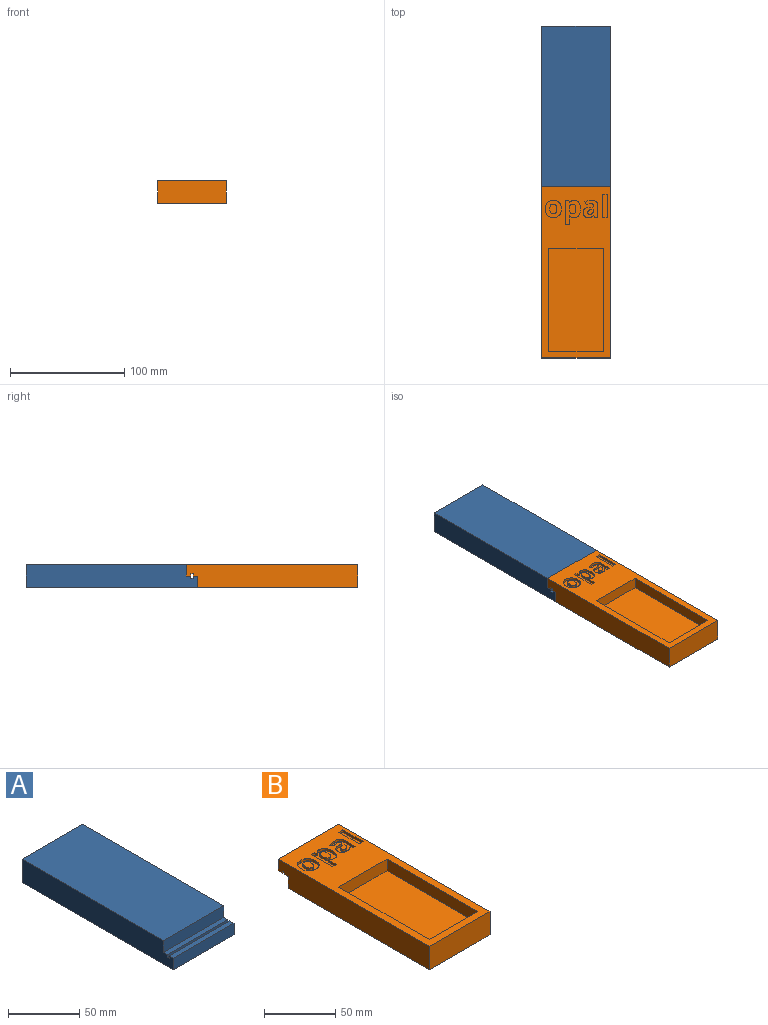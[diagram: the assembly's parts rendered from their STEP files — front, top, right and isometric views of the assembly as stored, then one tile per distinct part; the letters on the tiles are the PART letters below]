
ASSEMBLY  parts=2 mates=1
PART A: 12 faces, bbox 60x150x20 mm
  f0: plane 60x4mm, normal (0,0,1), area 240mm2, adj f1,f2,f5,f9
  f1: plane 150x20mm, normal (1,0,0), area 2896mm2, adj f0,f2,f3,f4,f6,f7,f8,f9
  f2: plane 60x10mm, normal (0,-1,0), area 600mm2, adj f0,f1,f5,f6
  f3: plane 140x60mm, normal (0,0,1), area 8400mm2, adj f1,f4,f5,f8
  f4: plane 60x20mm, normal (0,1,0), area 1200mm2, adj f1,f3,f5,f6
  f5: plane 150x20mm, normal (-1,0,0), area 2896mm2, adj f0,f2,f3,f4,f6,f7,f8,f9
  f6: plane 150x60mm, normal (0,0,-1), area 9000mm2, adj f1,f2,f4,f5
  f7: plane 60x4mm, normal (0,0,1), area 240mm2, adj f1,f5,f8,f10
  f8: plane 60x10mm, normal (0,-1,0), area 600mm2, adj f1,f3,f5,f7
  f9: plane 60x2mm, normal (0,1,0), area 120mm2, adj f0,f1,f5,f11
  f10: plane 60x2mm, normal (0,-1,0), area 120mm2, adj f1,f5,f7,f11
  f11: plane 60x2mm, normal (0,0,1), area 120mm2, adj f1,f5,f9,f10
PART B: 94 faces, bbox 60x150x20 mm
  f0: plane 60x4mm, normal (0,0,-1), area 240mm2, adj f1,f3,f4,f91
  f1: plane 150x20mm, normal (1,0,0), area 2896mm2, adj f0,f2,f3,f5,f6,f12,f13,f91
  f2: plane 150x60mm, normal (0,0,1), area 4078mm2, adj f1,f3,f4,f5,f7,f8,f9,f10
  f3: plane 60x10mm, normal (0,1,0), area 600mm2, adj f0,f1,f2,f4
  f4: plane 150x20mm, normal (-1,0,0), area 2896mm2, adj f0,f2,f3,f5,f6,f12,f13,f91
  f5: plane 60x20mm, normal (0,-1,0), area 1200mm2, adj f1,f2,f4,f6
  f6: plane 140x60mm, normal (0,0,-1), area 8400mm2, adj f1,f4,f5,f13
  f7: plane 48x10mm, normal (0,-1,0), area 480mm2, adj f2,f8,f10,f11
  f8: plane 90x10mm, normal (1,0,0), area 900mm2, adj f2,f7,f9,f11
  f9: plane 48x10mm, normal (0,1,0), area 480mm2, adj f2,f8,f10,f11
  f10: plane 90x10mm, normal (-1,0,0), area 900mm2, adj f2,f7,f9,f11
  f11: plane 90x48mm, normal (0,0,1), area 4320mm2, adj f7,f8,f9,f10
  f12: plane 60x4mm, normal (0,0,-1), area 240mm2, adj f1,f4,f13,f92
  f13: plane 60x10mm, normal (0,1,0), area 600mm2, adj f1,f4,f6,f12
  f14: plane 2x1.53mm, normal (-0.04,1,0), area 3.1mm2, adj f15,f38,f39,f89
  f15: plane 2x1.19mm, normal (1,0,0), area 2.4mm2, adj f14,f16,f39,f89
  f16: extruded ~2.1x2mm, area 4.6mm2, adj f15,f17,f39,f89
  f17: extruded ~2.2x2mm, area 4.8mm2, adj f16,f18,f39,f89
  f18: extruded ~2x1.92mm, area 5.8mm2, adj f17,f19,f39,f89
  f19: extruded ~2x1.74mm, area 4mm2, adj f18,f38,f39,f89
  f20: plane 2x1.97mm, normal (0.93,0.36,0), area 4.2mm2, adj f2,f21,f37,f39
  f21: plane 2.76x2mm, normal (0,1,0), area 5.5mm2, adj f2,f20,f22,f39
  f22: plane 9.65x2mm, normal (-1,0,0), area 19.3mm2, adj f2,f21,f23,f39
  f23: extruded ~3.86x2mm, area 8.6mm2, adj f2,f22,f24,f39
  f24: extruded ~4.47x2mm, area 9.5mm2, adj f2,f23,f25,f39
  f25: extruded ~5.54x2mm, area 11.5mm2, adj f2,f24,f26,f39
  f26: plane 2.67x2mm, normal (0.9,0.44,0), area 5.9mm2, adj f2,f25,f27,f39
  f27: extruded ~4.08x2mm, area 8.5mm2, adj f2,f26,f28,f39
  f28: extruded ~2.26x2.2mm, area 7.2mm2, adj f2,f27,f29,f39
  f29: plane 2x0.63mm, normal (1,0,0), area 1.3mm2, adj f2,f28,f30,f39
  f30: plane 2.52x2mm, normal (0.03,-1,0), area 5mm2, adj f2,f29,f31,f39
  f31: extruded ~4.86x2mm, area 10.1mm2, adj f2,f30,f32,f39
  f32: extruded ~3.4x2mm, area 7.9mm2, adj f2,f31,f33,f39
  f33: extruded ~3.4x2mm, area 7.4mm2, adj f2,f32,f34,f39
  f34: extruded ~3.28x2mm, area 7.2mm2, adj f2,f33,f35,f39
  f35: extruded ~2.75x2mm, area 5.6mm2, adj f2,f34,f36,f39
  f36: extruded ~2.05x2mm, area 5.4mm2, adj f2,f35,f37,f39
  f37: plane 2x0.1mm, normal (0,1,0), area 0.2mm2, adj f2,f20,f36,f39
  f38: extruded ~2.57x2mm, area 5.3mm2, adj f14,f19,f39,f89
  f39: plane 15.05x12.92mm, normal (0,0,1), area 128.6mm2, adj f14,f15,f16,f17,f18,f19,f20,f21
  f40: extruded ~2.14x2mm, area 4.8mm2, adj f41,f62,f63,f90
  f41: extruded ~2.05x2mm, area 4.9mm2, adj f40,f42,f63,f90
  f42: extruded ~3.21x2mm, area 6.6mm2, adj f41,f43,f63,f90
  f43: extruded ~4.38x2.66mm, area 11.6mm2, adj f42,f44,f63,f90
  f44: extruded ~2.2x2mm, area 5mm2, adj f43,f45,f63,f90
  f45: extruded ~3.34x2mm, area 6.9mm2, adj f44,f46,f63,f90
  f46: plane 2x0.43mm, normal (-1,0,0), area 0.9mm2, adj f45,f62,f63,f90
  f47: extruded ~4.01x2mm, area 9.2mm2, adj f2,f48,f61,f63
  f48: extruded ~2.95x2mm, area 6.3mm2, adj f2,f47,f49,f63
  f49: extruded ~2.61x2mm, area 6.6mm2, adj f2,f48,f50,f63
  f50: extruded ~4.03x2mm, area 8.2mm2, adj f2,f49,f51,f63
  f51: extruded ~5.51x2mm, area 11.6mm2, adj f2,f50,f52,f63
  f52: extruded ~4.02x2mm, area 9.3mm2, adj f2,f51,f53,f63
  f53: extruded ~4.11x2.15mm, area 9.7mm2, adj f2,f52,f54,f63
  f54: plane 2x0.18mm, normal (0,-1,0), area 0.4mm2, adj f2,f53,f55,f63
  f55: plane 2x1.88mm, normal (-0.96,-0.28,0), area 3.9mm2, adj f2,f54,f56,f63
  f56: plane 3.21x2mm, normal (0,-1,0), area 6.4mm2, adj f2,f55,f57,f63
  f57: plane 20.86x2mm, normal (1,0,0), area 41.7mm2, adj f2,f56,f58,f63
  f58: plane 3.95x2mm, normal (0,1,0), area 7.9mm2, adj f2,f57,f59,f63
  f59: plane 5.87x2mm, normal (-1,0,0), area 11.7mm2, adj f2,f58,f60,f63
  f60: extruded ~2.1x2mm, area 4.2mm2, adj f2,f59,f61,f63
  f61: plane 2x0.21mm, normal (0,1,0), area 0.4mm2, adj f2,f47,f60,f63
  f62: extruded ~2.97x2mm, area 6.2mm2, adj f40,f46,f63,f90
  f63: plane 21.13x13.53mm, normal (0,0,1), area 164.8mm2, adj f40,f41,f42,f43,f44,f45,f46,f47
  f64: extruded ~5.53x2mm, area 12mm2, adj f2,f65,f81,f82
  f65: extruded ~3.98x2mm, area 8.2mm2, adj f2,f64,f66,f82
  f66: extruded ~2.6x2.45mm, area 7.3mm2, adj f2,f65,f67,f82
  f67: extruded ~3.68x2mm, area 7.7mm2, adj f2,f66,f68,f82
  f68: extruded ~5.21x2mm, area 11.5mm2, adj f2,f67,f69,f82
  f69: extruded ~5.52x2mm, area 11.9mm2, adj f2,f68,f70,f82
  f70: extruded ~3.99x2mm, area 8.2mm2, adj f2,f69,f71,f82
  f71: extruded ~2.62x2.45mm, area 7.3mm2, adj f2,f70,f72,f82
  f72: extruded ~3.68x2mm, area 7.7mm2, adj f2,f71,f81,f82
  f73: extruded ~3.25x2mm, area 6.7mm2, adj f74,f80,f82,f83
  f74: extruded ~3.23x2mm, area 6.7mm2, adj f73,f75,f82,f83
  f75: extruded ~2.28x2mm, area 5.3mm2, adj f74,f76,f82,f83
  f76: extruded ~2.3x2mm, area 5.3mm2, adj f75,f77,f82,f83
  f77: extruded ~3.23x2mm, area 6.7mm2, adj f76,f78,f82,f83
  f78: extruded ~3.26x2mm, area 6.7mm2, adj f77,f79,f82,f83
  f79: extruded ~2.28x2mm, area 5.3mm2, adj f78,f80,f82,f83
  f80: extruded ~2.3x2mm, area 5.3mm2, adj f73,f79,f82,f83
  f81: extruded ~5.2x2mm, area 11.5mm2, adj f2,f64,f72,f82
  f82: plane 15.02x14.04mm, normal (0,0,1), area 128.5mm2, adj f64,f65,f66,f67,f68,f69,f70,f71
  f83: plane 8.66x5.98mm, normal (0,0,1), area 43.5mm2, adj f73,f74,f75,f76,f77,f78,f79,f80
  f84: plane 3.95x2mm, normal (0,1,0), area 7.9mm2, adj f2,f85,f87,f88
  f85: plane 20.16x2mm, normal (-1,0,0), area 40.3mm2, adj f2,f84,f86,f88
  f86: plane 3.95x2mm, normal (0,-1,0), area 7.9mm2, adj f2,f85,f87,f88
  f87: plane 20.16x2mm, normal (1,0,0), area 40.3mm2, adj f2,f84,f86,f88
  f88: plane 20.16x3.95mm, normal (0,0,1), area 79.7mm2, adj f84,f85,f86,f87
  f89: plane 4.94x4.08mm, normal (0,0,1), area 16.3mm2, adj f14,f15,f16,f17,f18,f19,f38
  f90: plane 8.66x5.55mm, normal (0,0,1), area 40.5mm2, adj f40,f41,f42,f43,f44,f45,f46,f62
  f91: plane 60x2mm, normal (0,-1,0), area 120mm2, adj f0,f1,f4,f93
  f92: plane 60x2mm, normal (0,1,0), area 120mm2, adj f1,f4,f12,f93
  f93: plane 60x2mm, normal (0,0,-1), area 120mm2, adj f1,f4,f91,f92
PLACE A t=(0.27,67.66,55.77)mm fixed
PLACE B t=(-5.26,-93.18,55.77)mm
MATE slider B.f3 <-> A.f8  axis (0,1,0) through (-18.91,-4.71,70.77)mm
